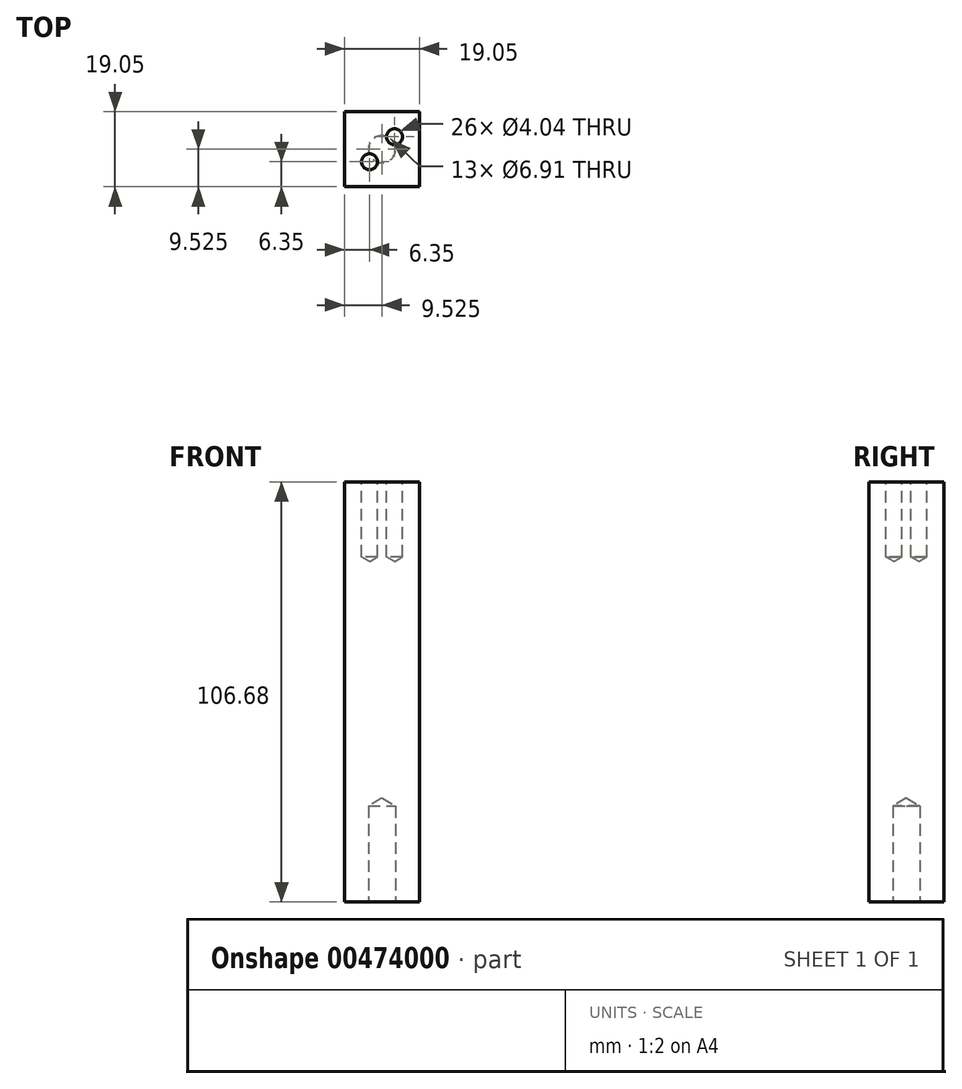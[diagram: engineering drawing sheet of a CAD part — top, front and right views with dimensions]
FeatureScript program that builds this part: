
annotation { "Feature Type Name" : "Feature", "Feature Type Description" : "" }
export const myFeature = defineFeature(function(context is Context, id is Id, definition is map)
    precondition{}
    {
        {
            var Q0;
            Q0=qCreatedBy(makeId("Top.planeOp"),FACE);
            var sketch = newSketch(context, id + "F0", { "sketchPlane" : qUnion([Q0])});
            skLineSegment(sketch, "E0.bottom", {"start": v(0, 0) * mm, "end": v(19.05, 0) * mm});
            skLineSegment(sketch, "E0.top", {"start": v(0, 19.05) * mm, "end": v(19.05, 19.05) * mm});
            skLineSegment(sketch, "E0.left", {"start": v(0, 0) * mm, "end": v(0, 19.05) * mm});
            skLineSegment(sketch, "E0.right", {"start": v(19.05, 0) * mm, "end": v(19.05, 19.05) * mm});
            skSolve(sketch);
        }
        {
            var Q0;
            Q0=makeQuery(id+"F0.imprint","IMPRINT",FACE,{"disambiguationData":[TD([[makeQuery(id+"F0.imprint","IMPRINT",EDGE,{"derivedFrom":sQuery(id+"F0.wireOp",EDGE,"E0.bottom")}),1.0]])]});
            extrude(context, id + "F1", {"entities" : qUnion([Q0]), "depth" : 106.68 * mm, "offsetDistance" : 25.4 * mm});
        }
        {
            var Q0;
            Q0=makeQuery(id+"F1.opExtrude","CAP_FACE",FACE,{"disambiguationData":[OSD([sQuery(id+"F0.wireOp",EDGE,"E0.bottom"),sQuery(id+"F0.wireOp",EDGE,"E0.top"),sQuery(id+"F0.wireOp",EDGE,"E0.left"),sQuery(id+"F0.wireOp",EDGE,"E0.right")])],"isStart":false});
            var sketch = newSketch(context, id + "F2", { "sketchPlane" : qUnion([Q0])});
            skPoint(sketch, "E1", {"position": v(12.7, 12.7) * mm});
            skPoint(sketch, "E2", {"position": v(6.35, 6.35) * mm});
            skSolve(sketch);
        }
        {
            var Q0;
            Q0=sQuery(id+"F2.wireOp",VERTEX,"E1");
            var Q1;
            Q1=sQuery(id+"F2.wireOp",VERTEX,"E2");
            var Q2;
            Q2=makeQuery(id+"F1.opExtrude","SWEPT_BODY",BODY,{"disambiguationData":[OSD([sQuery(id+"F0.wireOp",EDGE,"E0.bottom"),sQuery(id+"F0.wireOp",EDGE,"E0.top"),sQuery(id+"F0.wireOp",EDGE,"E0.left"),sQuery(id+"F0.wireOp",EDGE,"E0.right")])]});
            hole(context, id + "F3", {"style" : HoleStyle.SIMPLE, "endStyle" : HoleEndStyle.BLIND, "standardTappedOrClearance" : lookupTablePath({ "standard" : "ANSI", "engagement" : "75%", "pitch" : "32 tpi", "size" : "#10", "type" : "Tapped" }), "standardBlindInLast" : lookupTablePath({ "standard" : "ANSI", "engagement" : "75%", "pitch" : "32 tpi", "size" : "#10", "type" : "Tapped" }), "holeDiameter" : 4.04 * mm, "showTappedDepth" : true, "holeDepth" : 19.05 * mm, "isTappedThrough" : true, "tappedDepth" : 16.67 * mm, "tapClearance" : 3, "locations" : qUnion([Q0, Q1]), "scope" : qUnion([Q2]), "majorDiameter" : 4.83 * mm});
        }
        {
            var Q0;
            Q0=makeQuery(id+"F1.opExtrude","CAP_FACE",FACE,{"disambiguationData":[OSD([sQuery(id+"F0.wireOp",EDGE,"E0.bottom"),sQuery(id+"F0.wireOp",EDGE,"E0.top"),sQuery(id+"F0.wireOp",EDGE,"E0.left"),sQuery(id+"F0.wireOp",EDGE,"E0.right")])],"isStart":true});
            var sketch = newSketch(context, id + "F4", { "sketchPlane" : qUnion([Q0])});
            skLineSegment(sketch, "E3.0.0", {"start": v(0, -19.05) * mm, "end": v(19.05, -19.05) * mm});
            skLineSegment(sketch, "E3.0.1", {"start": v(19.05, -19.05) * mm, "end": v(19.05, 0) * mm});
            skLineSegment(sketch, "E3.0.2", {"start": v(19.05, 0) * mm, "end": v(0, 0) * mm});
            skLineSegment(sketch, "E3.0.3", {"start": v(0, 0) * mm, "end": v(0, -19.05) * mm});
            skPoint(sketch, "E4", {"position": v(9.52, -9.53) * mm});
            skPoint(sketch, "E5", {"position": v(9.52, 0) * mm});
            skSolve(sketch);
        }
        {
            var Q0;
            Q0=sQuery(id+"F4.wireOp",VERTEX,"E4");
            var Q1;
            Q1=makeQuery(id+"F1.opExtrude","SWEPT_BODY",BODY,{"disambiguationData":[OSD([sQuery(id+"F0.wireOp",EDGE,"E0.bottom"),sQuery(id+"F0.wireOp",EDGE,"E0.top"),sQuery(id+"F0.wireOp",EDGE,"E0.left"),sQuery(id+"F0.wireOp",EDGE,"E0.right")])]});
            hole(context, id + "F5", {"style" : HoleStyle.SIMPLE, "endStyle" : HoleEndStyle.BLIND, "standardTappedOrClearance" : lookupTablePath({ "standard" : "ANSI", "engagement" : "75%", "pitch" : "24 tpi", "size" : "5/16", "type" : "Tapped" }), "standardBlindInLast" : lookupTablePath({ "standard" : "ANSI", "engagement" : "75%", "pitch" : "24 tpi", "size" : "5/16", "type" : "Tapped" }), "holeDiameter" : 6.9 * mm, "showTappedDepth" : true, "holeDepth" : 24.34 * mm, "isTappedThrough" : true, "tappedDepth" : 21.17 * mm, "tapClearance" : 3, "locations" : qUnion([Q0]), "scope" : qUnion([Q1]), "majorDiameter" : 7.94 * mm});
        }
    });
